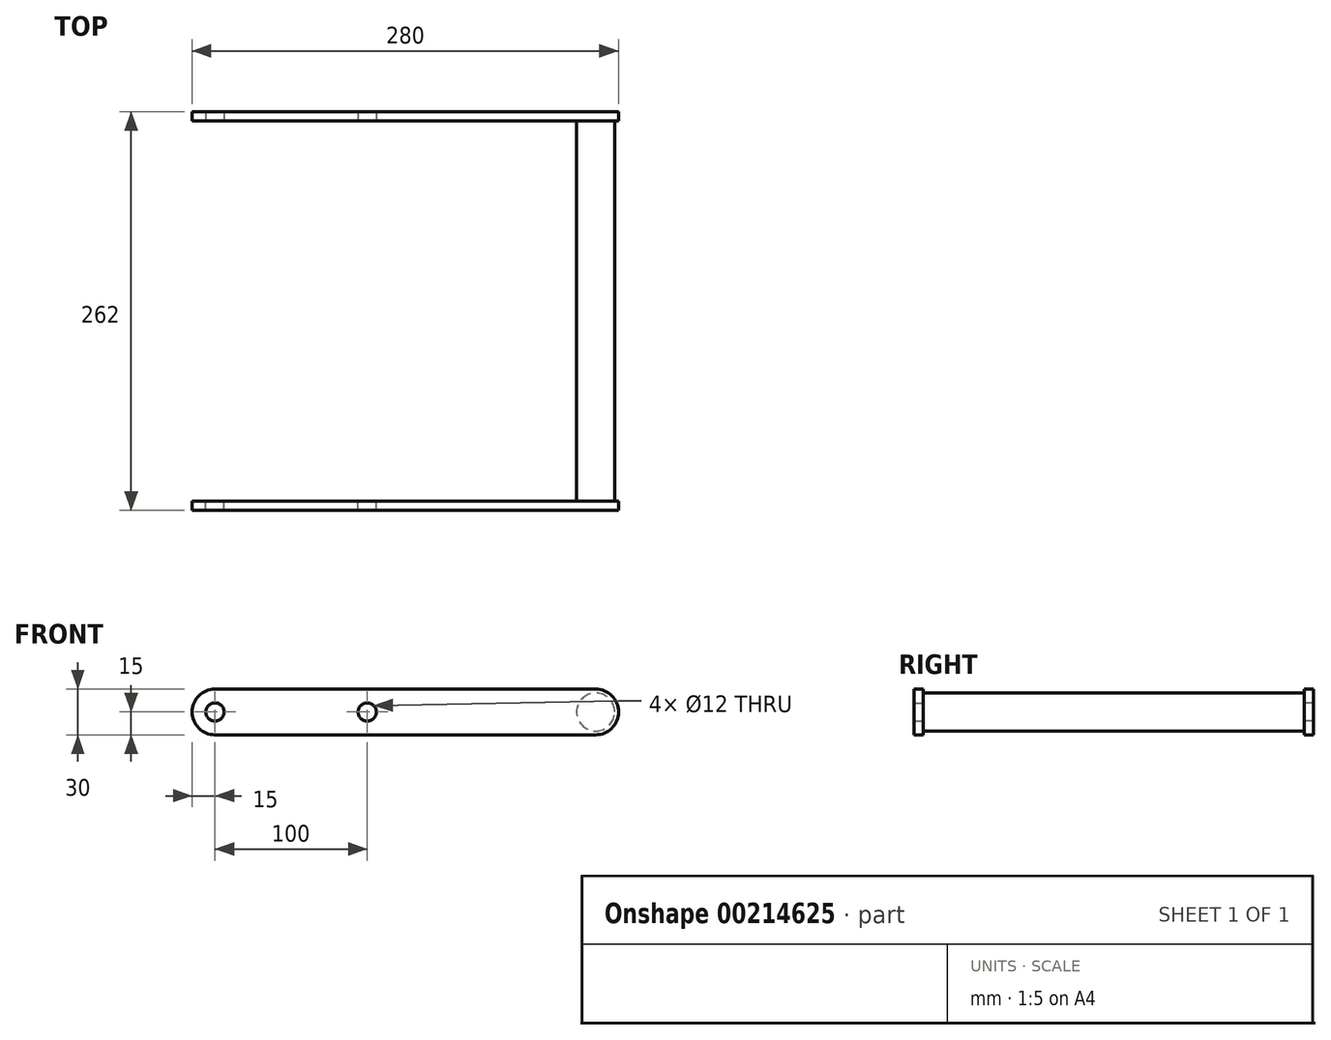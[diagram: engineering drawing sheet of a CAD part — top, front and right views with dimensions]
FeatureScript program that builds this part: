
annotation { "Feature Type Name" : "Feature", "Feature Type Description" : "" }
export const myFeature = defineFeature(function(context is Context, id is Id, definition is map)
    precondition{}
    {
        {
            var Q0;
            Q0=qCreatedBy(makeId("Front.planeOp"),FACE);
            cPlane(context, id + "F0", {"entities" : qUnion([Q0]), "cplaneType" : CPlaneType.OFFSET, "offset" : 125 * mm, "width" : 150 * mm, "height" : 150 * mm});
        }
        {
            var Q0;
            Q0=qCreatedBy(id+"F0.planeOp",FACE);
            var sketch = newSketch(context, id + "F1", { "sketchPlane" : qUnion([Q0])});
            skPoint(sketch, "E0.0", {"position": v(0, 0) * mm});
            skCircle(sketch, "E1", {"center": v(0, 0) * mm, "radius": 6 * mm});
            skArc(sketch, "E2", {"start": v(0, 15) * mm, "mid": v(-15, 0) * mm, "end": v(0, -15) * mm});
            skCircle(sketch, "E3", {"center": v(100, 0) * mm, "radius": 6 * mm});
            skArc(sketch, "E4", {"start": v(250, -15) * mm, "mid": v(265, 0) * mm, "end": v(250, 15) * mm});
            skLineSegment(sketch, "E5", {"start": v(0, 0) * mm, "end": v(250, 0) * mm, "construction": true});
            skLineSegment(sketch, "E6", {"start": v(0, 15) * mm, "end": v(250, 15) * mm});
            skLineSegment(sketch, "E7", {"start": v(250, -15) * mm, "end": v(0, -15) * mm});
            skCircle(sketch, "E8", {"center": v(250, 0) * mm, "radius": 12.5 * mm});
            skSolve(sketch);
        }
        {
            var Q0;
            Q0=makeQuery(id+"F1.imprint","IMPRINT",FACE,{"disambiguationData":[TD([[makeQuery(id+"F1.imprint","IMPRINT",EDGE,{"derivedFrom":sQuery(id+"F1.wireOp",EDGE,"E1")}),-1.0]])]});
            var Q1;
            Q1=makeQuery(id+"F1.imprint","IMPRINT",FACE,{"disambiguationData":[TD([[makeQuery(id+"F1.imprint","IMPRINT",EDGE,{"derivedFrom":sQuery(id+"F1.wireOp",EDGE,"E8")}),1.0]])]});
            extrude(context, id + "F2", {"entities" : qUnion([Q0, Q1]), "depth" : 6 * mm});
        }
        {
            var Q0;
            Q0=makeQuery(id+"F1.imprint","IMPRINT",FACE,{"disambiguationData":[TD([[makeQuery(id+"F1.imprint","IMPRINT",EDGE,{"derivedFrom":sQuery(id+"F1.wireOp",EDGE,"E8")}),1.0]])]});
            var Q1;
            Q1=qCreatedBy(makeId("Front.planeOp"),FACE);
            extrude(context, id + "F3", {"entities" : qUnion([Q0]), "operationType" : NewBodyOperationType.ADD, "endBound" : BoundingType.UP_TO_SURFACE, "oppositeDirection" : true, "endBoundEntityFace" : qUnion([Q1]), "depth" : 25 * mm});
        }
        {
            var Q0;
            Q0=makeQuery(id+"F2.opExtrude","SWEPT_BODY",BODY,{"disambiguationData":[OSD([sQuery(id+"F1.wireOp",EDGE,"E1"),sQuery(id+"F1.wireOp",EDGE,"E2"),sQuery(id+"F1.wireOp",EDGE,"E3"),sQuery(id+"F1.wireOp",EDGE,"E4"),sQuery(id+"F1.wireOp",EDGE,"E6"),sQuery(id+"F1.wireOp",EDGE,"E7")])]});
            var Q1;
            Q1=qCreatedBy(makeId("Front.planeOp"),FACE);
            mirror(context, id + "F4", {"operationType" : NewBodyOperationType.ADD, "entities" : qUnion([Q0]), "mirrorPlane" : qUnion([Q1])});
        }
    });
